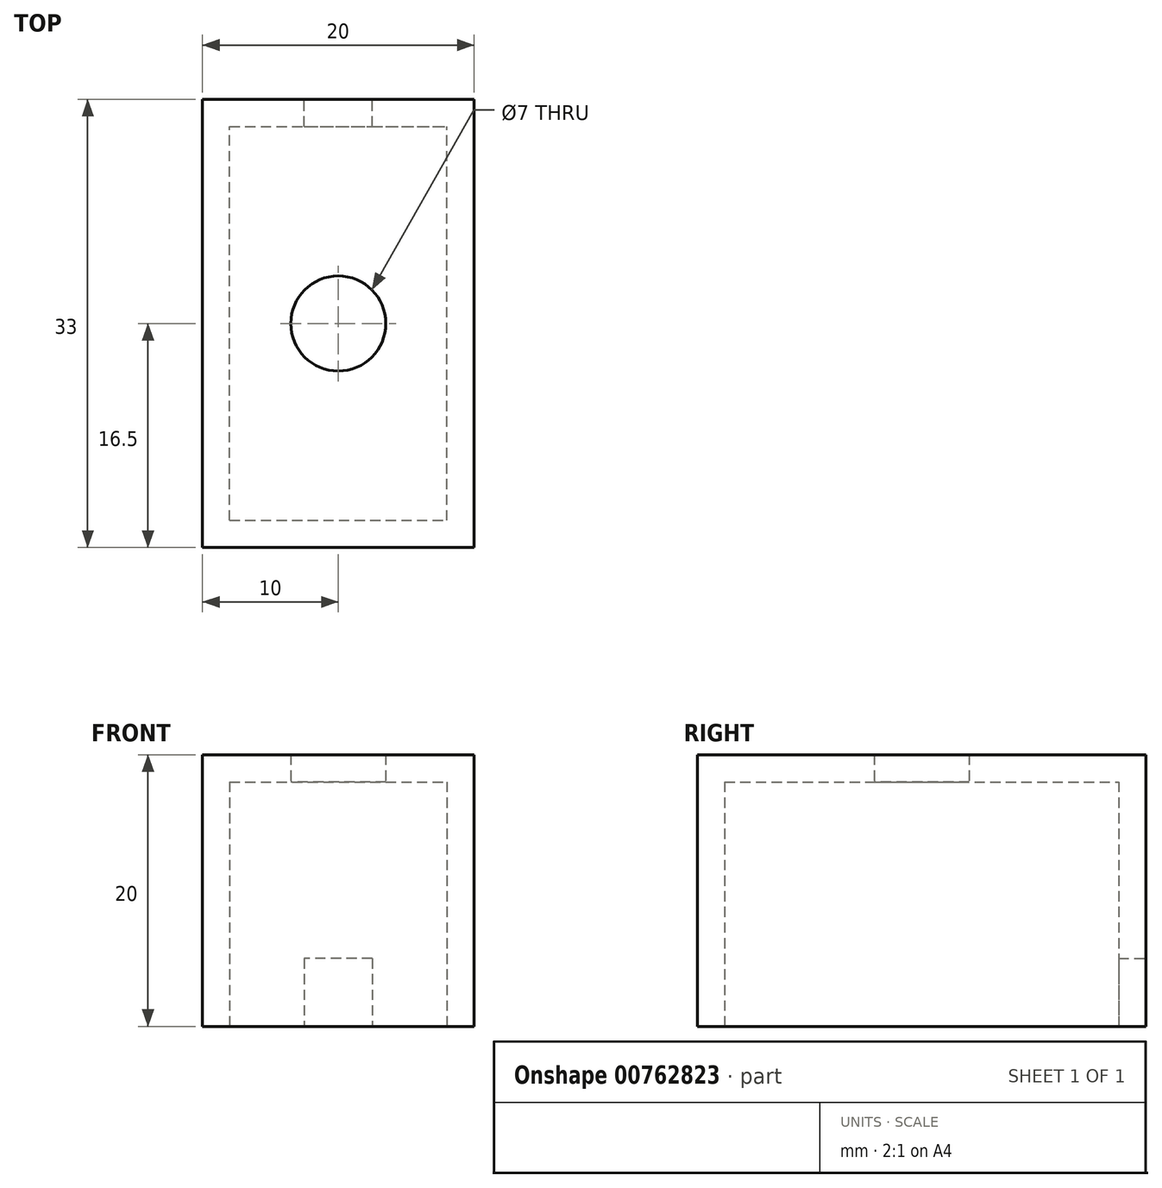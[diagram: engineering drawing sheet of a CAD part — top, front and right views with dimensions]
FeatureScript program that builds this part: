
annotation { "Feature Type Name" : "Feature", "Feature Type Description" : "" }
export const myFeature = defineFeature(function(context is Context, id is Id, definition is map)
    precondition{}
    {
        {
            var Q0;
            Q0=qCreatedBy(makeId("Top.planeOp"),FACE);
            var sketch = newSketch(context, id + "F0", { "sketchPlane" : qUnion([Q0])});
            skLineSegment(sketch, "E0.bottom", {"start": v(0, 0) * mm, "end": v(-20, 0) * mm});
            skLineSegment(sketch, "E0.top", {"start": v(0, 33) * mm, "end": v(-20, 33) * mm});
            skLineSegment(sketch, "E0.left", {"start": v(0, 0) * mm, "end": v(0, 33) * mm});
            skLineSegment(sketch, "E0.right", {"start": v(-20, 0) * mm, "end": v(-20, 33) * mm});
            skCircle(sketch, "E1", {"center": v(-10, 16.5) * mm, "radius": 3.5 * mm});
            skSolve(sketch);
        }
        {
            var Q0;
            Q0=makeQuery(id+"F0.imprint","IMPRINT",FACE,{"disambiguationData":[TD([[makeQuery(id+"F0.imprint","IMPRINT",EDGE,{"derivedFrom":sQuery(id+"F0.wireOp",EDGE,"E0.bottom")}),-1.0]])]});
            extrude(context, id + "F1", {"entities" : qUnion([Q0]), "depth" : 20 * mm, "offsetDistance" : 25 * mm});
        }
        {
            var Q0;
            Q0=makeQuery(id+"F1.opExtrude","CAP_FACE",FACE,{"disambiguationData":[OSD([sQuery(id+"F0.wireOp",EDGE,"E0.bottom"),sQuery(id+"F0.wireOp",EDGE,"E0.top"),sQuery(id+"F0.wireOp",EDGE,"E0.left"),sQuery(id+"F0.wireOp",EDGE,"E0.right"),sQuery(id+"F0.wireOp",EDGE,"E1")])],"isStart":true});
            var sketch = newSketch(context, id + "F2", { "sketchPlane" : qUnion([Q0])});
            skLineSegment(sketch, "E2.bottom", {"start": v(-18, -2) * mm, "end": v(-2, -2) * mm});
            skLineSegment(sketch, "E2.top", {"start": v(-18, -31) * mm, "end": v(-2, -31) * mm});
            skLineSegment(sketch, "E2.left", {"start": v(-18, -2) * mm, "end": v(-18, -31) * mm});
            skLineSegment(sketch, "E2.right", {"start": v(-2, -2) * mm, "end": v(-2, -31) * mm});
            skSolve(sketch);
        }
        {
            var Q0;
            Q0=makeQuery(id+"F2.imprint","IMPRINT",FACE,{"disambiguationData":[TD([[makeQuery(id+"F2.imprint","IMPRINT",EDGE,{"derivedFrom":sQuery(id+"F2.wireOp",EDGE,"E2.bottom")}),-1.0]])]});
            extrude(context, id + "F3", {"entities" : qUnion([Q0]), "operationType" : NewBodyOperationType.REMOVE, "oppositeDirection" : true, "depth" : 18 * mm, "offsetDistance" : 25 * mm});
        }
        {
            var Q0;
            Q0=makeQuery(id+"F1.opExtrude","CAP_FACE",FACE,{"disambiguationData":[OSD([sQuery(id+"F0.wireOp",EDGE,"E0.bottom"),sQuery(id+"F0.wireOp",EDGE,"E0.top"),sQuery(id+"F0.wireOp",EDGE,"E0.left"),sQuery(id+"F0.wireOp",EDGE,"E0.right"),sQuery(id+"F0.wireOp",EDGE,"E1")])],"isStart":true});
            var sketch = newSketch(context, id + "F4", { "sketchPlane" : qUnion([Q0])});
            skLineSegment(sketch, "E3.bottom", {"start": v(-12.5, -31) * mm, "end": v(-7.5, -31) * mm});
            skLineSegment(sketch, "E3.top", {"start": v(-12.5, -33) * mm, "end": v(-7.5, -33) * mm});
            skLineSegment(sketch, "E3.left", {"start": v(-12.5, -31) * mm, "end": v(-12.5, -33) * mm});
            skLineSegment(sketch, "E3.right", {"start": v(-7.5, -31) * mm, "end": v(-7.5, -33) * mm});
            skSolve(sketch);
        }
        {
            var Q0;
            Q0 = qSketchRegion(id + "F4", true);
            extrude(context, id + "F5", {"entities" : qUnion([Q0]), "operationType" : NewBodyOperationType.REMOVE, "oppositeDirection" : true, "depth" : 5 * mm, "offsetDistance" : 25 * mm});
        }
    });
